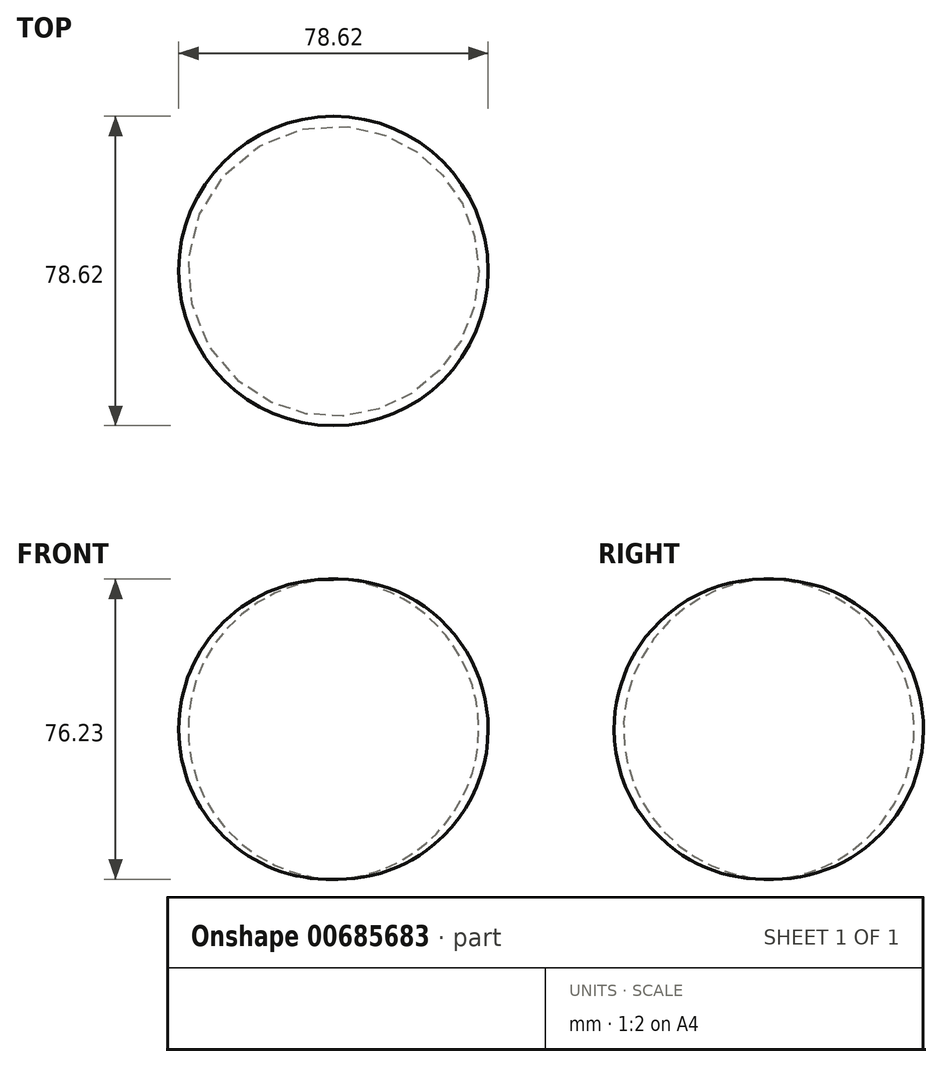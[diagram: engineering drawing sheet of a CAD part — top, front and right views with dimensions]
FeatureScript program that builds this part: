
annotation { "Feature Type Name" : "Feature", "Feature Type Description" : "" }
export const myFeature = defineFeature(function(context is Context, id is Id, definition is map)
    precondition{}
    {
        {
            var Q0;
            Q0=qCreatedBy(makeId("Front.planeOp"),FACE);
            var sketch = newSketch(context, id + "F0", { "sketchPlane" : qUnion([Q0])});
            skLineSegment(sketch, "E0", {"start": v(0, -32.58) * mm, "end": v(0, 43.62) * mm});
            skArc(sketch, "E1", {"start": v(0, -32.58) * mm, "mid": v(39.31, 5.52) * mm, "end": v(0, 43.62) * mm});
            skSolve(sketch);
        }
        {
            var Q0;
            Q0=makeQuery(id+"F0.imprint","IMPRINT",FACE,{"disambiguationData":[TD([[makeQuery(id+"F0.imprint","IMPRINT",EDGE,{"derivedFrom":sQuery(id+"F0.wireOp",EDGE,"E0")}),-1.0]])]});
            var sketch = newSketch(context, id + "F1", { "sketchPlane" : qUnion([Q0])});
            skSolve(sketch);
        }
        {
            var Q0;
            Q0=makeQuery(id+"F1.imprint","IMPRINT",FACE,{"disambiguationData":[TD([[makeQuery(id+"F1.imprint","IMPRINT",EDGE,{"derivedFrom":makeQuery(id+"F0.imprint","IMPRINT",EDGE,{"derivedFrom":sQuery(id+"F0.wireOp",EDGE,"E0")})}),-1.0]])]});
            var Q1;
            Q1=sQuery(id+"F0.wireOp",EDGE,"E0");
            revolve(context, id + "F2", {"entities" : qUnion([Q0]), "axis" : qUnion([Q1]), "revolveType" : RevolveType.FULL});
        }
    });
